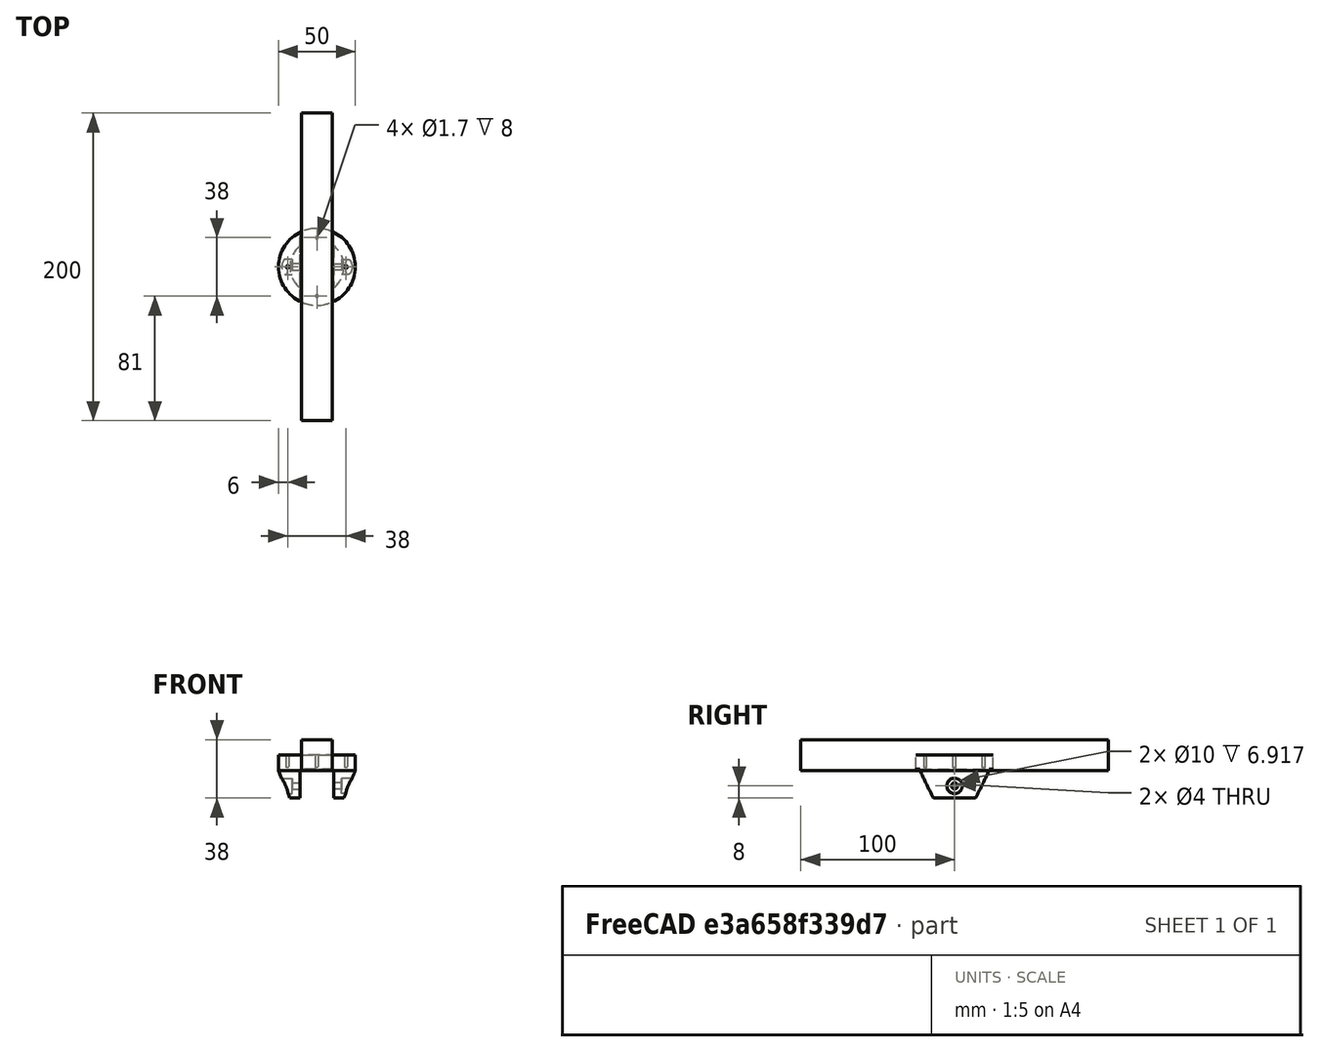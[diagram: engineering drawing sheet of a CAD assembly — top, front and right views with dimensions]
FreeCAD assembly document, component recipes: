
FREECAD ASSEMBLY — COMPONENT RECIPES ("keyboard_chair_attachment_rev1")

This assembly document has 2 components, labeled P0..P1 below (a component is one placed body or linked part). 2 of them carry a construction recipe — the FreeCAD feature program that regenerates the part from scratch, quoted from this document or its linked companion documents; the rest are supplied as boundary geometry only. No exploded tour is included for this assembly.
COMPONENT P0 — recipe-attached ("Extruded Bar", modeled in this document).
Construction recipe (the document's own serialized feature program — sketch geometry with constraints, then the solid features built on it; lengths are millimeters unless a unit is written):

FEATURE [Sketcher::SketchObject] Sketch  label="Extruded Bar Extrusion"
  FullyConstrained = true
  MapMode = 5
  Placement = pos=(0,0,0) rot=(1,0,0;1.5708rad)
  Support = -> [XZ_Plane002]
  expr: Constraints[10] = Variables.extruded_bar_height
  expr: Constraints[11] = Variables.extruded_bar_width
  sketch-geometry (5):
    g0: LineSegment StartX=-10 StartY=-10 StartZ=0 EndX=-10 EndY=10 EndZ=0
    g1: LineSegment StartX=-10 StartY=10 StartZ=0 EndX=10 EndY=10 EndZ=0
    g2: LineSegment StartX=10 StartY=10 StartZ=0 EndX=10 EndY=-10 EndZ=0
    g3: LineSegment StartX=10 StartY=-10 StartZ=0 EndX=-10 EndY=-10 EndZ=0
    g4: GeomPoint X=0 Y=0 Z=0
  constraints (12):
    c: Coincident(g0,g1)
    c: Coincident(g1,g2)
    c: Coincident(g2,g3)
    c: Coincident(g3,g0)
    c: Horizontal(g1)
    c: Horizontal(g3)
    c: Vertical(g0)
    c: Vertical(g2)
    c: Symmetric(g1,g0,g4)
    c: Coincident(g4,g-1)
    c: DistanceY(g2,g2) = 20
    c: DistanceX(g1,g1) = 20
FEATURE [PartDesign::Pad] Pad  label="Extruded Bar Outer"
  Direction = (0,-1,2e-16)
  Length = 200
  Length2 = 10
  Midplane = true
  Placement = pos=(0,0,0) rot=(1,0,0;1.5708rad)
  Profile = -> Sketch
  ReferenceAxis = -> Sketch [N_Axis]
  Type = 0
  expr: Length = Variables.extruded_bar_length
FEATURE [PartDesign::Body] Extruded_Bar_Body  label="Extruded Bar Body"
  Group = -> [Sketch,Pad]
  Origin = -> Origin002
  Tip = -> Pad
COMPONENT P1 — recipe-attached ("Keyboard Mount", modeled in this document).
Construction recipe (the document's own serialized feature program — sketch geometry with constraints, then the solid features built on it; lengths are millimeters unless a unit is written):

FEATURE [PartDesign::CoordinateSystem] LCS_003
  AttacherType = Attacher::AttachEngine3D
  MapMode = 2
  Support = -> [X_Axis004]
FEATURE [PartDesign::Plane] DatumPlane  label="Keyboard Mount Top"
  Length = 60
  MapMode = 5
  ResizeMode = 0
  Support = -> [XY_Plane004]
  Width = 60
FEATURE [PartDesign::Plane] DatumPlane001  label="Keyboard Mount Mid"
  AttachmentOffset = pos=(0,0,-10) rot=(0,0,1;0rad)
  Length = 60
  MapMode = 5
  Placement = pos=(0,0,-10) rot=(0,0,1;0rad)
  ResizeMode = 0
  Support = -> [DatumPlane]
  Width = 60
FEATURE [PartDesign::Plane] DatumPlane002  label="Keyboard Mount Bottom"
  AttachmentOffset = pos=(0,0,-18) rot=(0,0,1;0rad)
  Length = 60
  MapMode = 5
  Placement = pos=(0,0,-28) rot=(0,0,1;0rad)
  ResizeMode = 0
  Support = -> [DatumPlane001]
  Width = 60
FEATURE [Sketcher::SketchObject] Sketch001
  FullyConstrained = true
  MapMode = 5
  Support = -> [DatumPlane]
  sketch-geometry (1):
    g0: Circle CenterX=0 CenterY=0 CenterZ=0 NormalX=0 NormalY=0 NormalZ=1 AngleXU=0 Radius=25
  constraints (2):
    c: Coincident(g0,g-1)
    c: Diameter(g0) = 50
FEATURE [PartDesign::Pad] Pad001  label="Keyboard Mount Upper Section"
  Direction = (0,0,1)
  Length = 10
  Length2 = 10
  Profile = -> Sketch001
  ReferenceAxis = -> Sketch001 [N_Axis]
  Type = 3
  UpToFace = -> DatumPlane001
FEATURE [Sketcher::SketchObject] Sketch002
  FullyConstrained = true
  MapMode = 5
  Placement = pos=(0,0,-10) rot=(0,0,1;0rad)
  Support = -> [DatumPlane001]
  expr: Constraints[1] = 50
  sketch-geometry (1):
    g0: Circle CenterX=0 CenterY=0 CenterZ=0 NormalX=0 NormalY=0 NormalZ=1 AngleXU=0 Radius=25
  constraints (2):
    c: Coincident(g0,g-1)
    c: Diameter(g0) = 50
FEATURE [Sketcher::SketchObject] Sketch003
  FullyConstrained = true
  MapMode = 5
  Placement = pos=(0,0,-28) rot=(0,0,1;0rad)
  Support = -> [DatumPlane002]
  sketch-geometry (1):
    g0: Circle CenterX=0 CenterY=0 CenterZ=0 NormalX=0 NormalY=0 NormalZ=1 AngleXU=0 Radius=17.5
  constraints (2):
    c: Coincident(g0,g-1)
    c: Diameter(g0) = 35
FEATURE [PartDesign::AdditiveLoft] AdditiveLoft  label="Keyboard Mount Lower Section"
  BaseFeature = -> Pad001
  Closed = false
  Profile = -> Sketch003
  Ruled = false
  Sections = -> [Sketch002]
FEATURE [PartDesign::Plane] DatumPlane003  label="Keyboard Mount Tenting Puck Hole Depth"
  AttachmentOffset = pos=(0,0,-8) rot=(0,0,1;0rad)
  Length = 60
  MapMode = 5
  Placement = pos=(0,0,-8) rot=(0,0,1;0rad)
  ResizeMode = 0
  Support = -> [DatumPlane]
  Width = 60
FEATURE [Sketcher::SketchObject] Sketch004
  FullyConstrained = true
  MapMode = 5
  Support = -> [DatumPlane]
  sketch-geometry (5):
    g0: Circle CenterX=0 CenterY=0 CenterZ=0 NormalX=0 NormalY=0 NormalZ=1 AngleXU=0 Radius=19
    g1: Circle CenterX=0 CenterY=19 CenterZ=0 NormalX=0 NormalY=0 NormalZ=1 AngleXU=0 Radius=0.85
    g2: Circle CenterX=19 CenterY=0 CenterZ=0 NormalX=0 NormalY=0 NormalZ=1 AngleXU=0 Radius=0.85
    g3: Circle CenterX=0 CenterY=-19 CenterZ=0 NormalX=0 NormalY=0 NormalZ=1 AngleXU=0 Radius=0.85
    g4: Circle CenterX=-19 CenterY=0 CenterZ=0 NormalX=0 NormalY=0 NormalZ=1 AngleXU=0 Radius=0.85
  constraints (14):
    c: Coincident(g0,g-1)
    c: PointOnObject(g1,g0)
    c: PointOnObject(g2,g0)
    c: PointOnObject(g3,g0)
    c: PointOnObject(g4,g0)
    c: PointOnObject(g4,g-1)
    c: PointOnObject(g1,g-2)
    c: PointOnObject(g2,g-1)
    c: PointOnObject(g3,g-2)
    c: Equal(g1,g2)
    c: Equal(g2,g3)
    c: Equal(g3,g4)
    c: Diameter(g1) = 1.7
    c: Diameter(g0) = 38
FEATURE [PartDesign::Pocket] Pocket  label="Keyboard Mount Tenting Puck Holes"
  BaseFeature = -> AdditiveLoft
  Direction = (0,0,-1)
  Length = 0
  Length2 = 5
  Profile = -> Sketch004
  ReferenceAxis = -> Sketch004 [N_Axis]
  Type = 3
  UpToFace = -> DatumPlane003 [Plane]
FEATURE [Sketcher::SketchObject] Sketch005
  FullyConstrained = true
  MapMode = 5
  Placement = pos=(0,0,0) rot=(1,0,0;1.5708rad)
  Support = -> [XZ_Plane004]
  expr: .Constraints.height = Variables.extruded_bar_height + 2
  expr: .Constraints.width = Variables.extruded_bar_width + 2
  sketch-geometry (5):
    g0: LineSegment StartX=-11 StartY=-31 StartZ=0 EndX=-11 EndY=-9 EndZ=0
    g1: LineSegment StartX=-11 StartY=-9 StartZ=0 EndX=11 EndY=-9 EndZ=0
    g2: LineSegment StartX=11 StartY=-9 StartZ=0 EndX=11 EndY=-31 EndZ=0
    g3: LineSegment StartX=11 StartY=-31 StartZ=0 EndX=-11 EndY=-31 EndZ=0
    g4: GeomPoint X=0 Y=-20 Z=0
  constraints (13):
    c: Coincident(g0,g1)
    c: Coincident(g1,g2)
    c: Coincident(g2,g3)
    c: Coincident(g3,g0)
    c: Horizontal(g1)
    c: Horizontal(g3)
    c: Vertical(g0)
    c: Vertical(g2)
    c: Symmetric(g1,g0,g4)
    c: PointOnObject(g4,g-2)
    c: DistanceX(g1,g1) = 22  'width'
    c: DistanceY(g2,g2) = 22  'height'
    c: DistanceY(g4,g-1) = 20  'offset'
FEATURE [PartDesign::Pocket] Pocket001  label="Keyboard Mount Bar Cutout"
  BaseFeature = -> Pocket
  Direction = (0,1,2e-16)
  Length = 5
  Length2 = 5
  Midplane = true
  Profile = -> Sketch005
  ReferenceAxis = -> Sketch005 [N_Axis]
  Type = 1
FEATURE [PartDesign::Plane] DatumPlane004  label="Keyboard Mount Bar Side Right"
  AttachmentOffset = pos=(0,0,11) rot=(0,0,1;0rad)
  Length = 60.2956
  MapMode = 5
  Placement = pos=(11,-2.4e-15,2.4e-15) rot=(0.57735,0.57735,0.57735;2.0944rad)
  ResizeMode = 0
  Support = -> [YZ_Plane004]
  Width = 63.2956
  expr: .AttachmentOffset.Base.z = Sketch005.Constraints.width / 2
FEATURE [Sketcher::SketchObject] Sketch006
  FullyConstrained = true
  MapMode = 5
  Placement = pos=(11,-2.4e-15,2.4e-15) rot=(0.57735,0.57735,0.57735;2.0944rad)
  Support = -> [DatumPlane004]
  expr: .Constraints.offset = Sketch005.Constraints.offset
  sketch-geometry (1):
    g0: Circle CenterX=0 CenterY=-20 CenterZ=0 NormalX=0 NormalY=0 NormalZ=1 AngleXU=0 Radius=2
  constraints (3):
    c: PointOnObject(g0,g-2)
    c: DistanceY(g0,g-1) = 20  'offset'
    c: Diameter(g0) = 4  'hole_diam'
FEATURE [PartDesign::Pocket] Pocket002  label="Keyboard Mount Bar Screw Cutout Right"
  BaseFeature = -> Pocket001
  Direction = (-1,1e-16,-1e-16)
  Length = 5
  Length2 = 5
  Profile = -> Sketch006
  ReferenceAxis = -> Sketch006 [N_Axis]
  Reversed = true
  Type = 1
FEATURE [PartDesign::Plane] DatumPlane005  label="Keyboard Mount Bar Mount Screw Head Right"
  AttachmentOffset = pos=(0,0,5) rot=(0,0,1;0rad)
  Length = 60.2956
  MapMode = 5
  Placement = pos=(16,-3e-15,3e-15) rot=(0.57735,0.57735,0.57735;2.0944rad)
  ResizeMode = 0
  Support = -> [DatumPlane004]
  Width = 63.2956
FEATURE [Sketcher::SketchObject] Sketch007
  FullyConstrained = true
  MapMode = 5
  Placement = pos=(16,-3e-15,3e-15) rot=(0.57735,0.57735,0.57735;2.0944rad)
  Support = -> [DatumPlane005]
  expr: .Constraints.offset = Sketch005.Constraints.offset
  sketch-geometry (1):
    g0: Circle CenterX=0 CenterY=-20 CenterZ=0 NormalX=0 NormalY=0 NormalZ=1 AngleXU=0 Radius=5
  constraints (3):
    c: PointOnObject(g0,g-2)
    c: DistanceY(g0,g-1) = 20  'offset'
    c: Diameter(g0) = 10  'hole_diam'
FEATURE [PartDesign::Pocket] Pocket003  label="Keyboard Mount Bar Screw Head Cutout Right"
  BaseFeature = -> Pocket002
  Direction = (-1,0,0)
  Length = 5
  Length2 = 5
  Profile = -> Sketch007
  ReferenceAxis = -> Sketch007 [N_Axis]
  Reversed = true
  Type = 1
FEATURE [PartDesign::CoordinateSystem] Local_CS  label="Keyboard Mount Body Bar"
  AttacherType = Attacher::AttachEngine3D
  AttachmentOffset = pos=(0,0,-20) rot=(0,0,1;0rad)
  MapMode = 5
  Placement = pos=(0,0,-20) rot=(0,0,1;0rad)
  Support = -> [LCS_003]
  expr: .AttachmentOffset.Base.z = -Sketch005.Constraints.offset
FEATURE [PartDesign::Plane] DatumPlane006  label="Keyboard Mount Bar Side Left"
  AttachmentOffset = pos=(0,0,-11) rot=(0,0,1;0rad)
  Length = 60.2956
  MapMode = 5
  Placement = pos=(-11,2.4e-15,-2.4e-15) rot=(0.57735,0.57735,0.57735;2.0944rad)
  ResizeMode = 0
  Support = -> [YZ_Plane004]
  Width = 63.2956
  expr: .AttachmentOffset.Base.z = -Sketch005.Constraints.width / 2
FEATURE [PartDesign::Plane] DatumPlane007  label="Keyboard Mount Bar Mount Screw Head Left"
  AttachmentOffset = pos=(0,0,-5) rot=(0,0,1;0rad)
  Length = 60.2956
  MapMode = 5
  Placement = pos=(-16,3e-15,-3e-15) rot=(0.57735,0.57735,0.57735;2.0944rad)
  ResizeMode = 0
  Support = -> [DatumPlane006]
  Width = 63.2956
FEATURE [Sketcher::SketchObject] Sketch008
  FullyConstrained = true
  MapMode = 5
  Placement = pos=(-11,2.4e-15,-2.4e-15) rot=(0.57735,0.57735,0.57735;2.0944rad)
  Support = -> [DatumPlane006]
  expr: Constraints[1] = Sketch006.Constraints.hole_diam
  expr: Constraints[2] = Sketch006.Constraints.offset
  sketch-geometry (1):
    g0: Circle CenterX=0 CenterY=-20 CenterZ=0 NormalX=0 NormalY=0 NormalZ=1 AngleXU=0 Radius=2
  constraints (3):
    c: PointOnObject(g0,g-2)
    c: Diameter(g0) = 4
    c: DistanceY(g0,g-1) = 20
FEATURE [PartDesign::Pocket] Pocket004  label="Keyboard Mount Bar Screw Cutout Left"
  BaseFeature = -> Pocket003
  Direction = (-1,1e-16,-1e-16)
  Length = 5
  Length2 = 5
  Profile = -> Sketch008
  ReferenceAxis = -> Sketch008 [N_Axis]
  Type = 1
FEATURE [Sketcher::SketchObject] Sketch009
  FullyConstrained = true
  MapMode = 5
  Placement = pos=(-16,3e-15,-3e-15) rot=(0.57735,0.57735,0.57735;2.0944rad)
  Support = -> [DatumPlane007]
  expr: Constraints[1] = Sketch007.Constraints.offset
  expr: Constraints[2] = Sketch007.Constraints.hole_diam
  sketch-geometry (1):
    g0: Circle CenterX=0 CenterY=-20 CenterZ=0 NormalX=0 NormalY=0 NormalZ=1 AngleXU=0 Radius=5
  constraints (3):
    c: PointOnObject(g0,g-2)
    c: DistanceY(g0,g-1) = 20
    c: Diameter(g0) = 10
FEATURE [PartDesign::Pocket] Pocket005  label="Keyboard Mount Bar Screw Head Cutout Left"
  BaseFeature = -> Pocket004
  Direction = (-1,0,0)
  Length = 0
  Length2 = 5
  Profile = -> Sketch009
  ReferenceAxis = -> Sketch009 [N_Axis]
  Type = 1
FEATURE [PartDesign::Body] Keyboard_Mount_Body  label="Keyboard Mount Body"
  Group = -> [LCS_003,DatumPlane,DatumPlane001,DatumPlane002,Sketch001,Pad001,Sketch002,Sketch003,AdditiveLoft,DatumPlane003,Sketch004,Pocket,Sketch005,Pocket001,DatumPlane004,Sketch006,Pocket002,DatumPlane005,Sketch007,Pocket003,Local_CS,DatumPlane006,Sketch008,Pocket004,DatumPlane007,Sketch009,Pocket005]
  Origin = -> Origin004
  Tip = -> Pocket005
PROVENANCE & LICENSES
A FreeCAD (.FCStd) document from a public repository crawl; recipes are the document's own serialized feature recipes (and, for linked parts, companion documents' recipes).
License: as declared in the source repository (recorded in the dataset sidecar).
